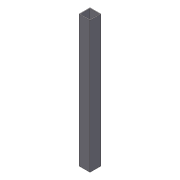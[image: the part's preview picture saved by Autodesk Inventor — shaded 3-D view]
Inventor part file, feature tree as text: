
AUTODESK INVENTOR PART (.ipt)
format: ipt  version: 2012 (Build 160160000, 160)  size: 71,168 bytes
history: native  units: in
note: dims shown in document units (in); Inventor stores cm internally (conversion verified against a paired STEP export)
features: extrude x1, shell x1, sketch x1
ambient origin geometry x8: Origin, YZ Plane, XZ Plane, XY Plane, X Axis, Y Axis, Z Axis, Center Point
bodies: Solid1 (feature_tree)
feature tree (3):
  extrude  "Extrusion1"  Depth=12.0in
  shell  "Shell1"  Thickness=1.0in
  sketch  "Sketch1"  dims[d0=1.0in d1=12.0in d2=1.0in d3=0.0in d4=0.0625in]
